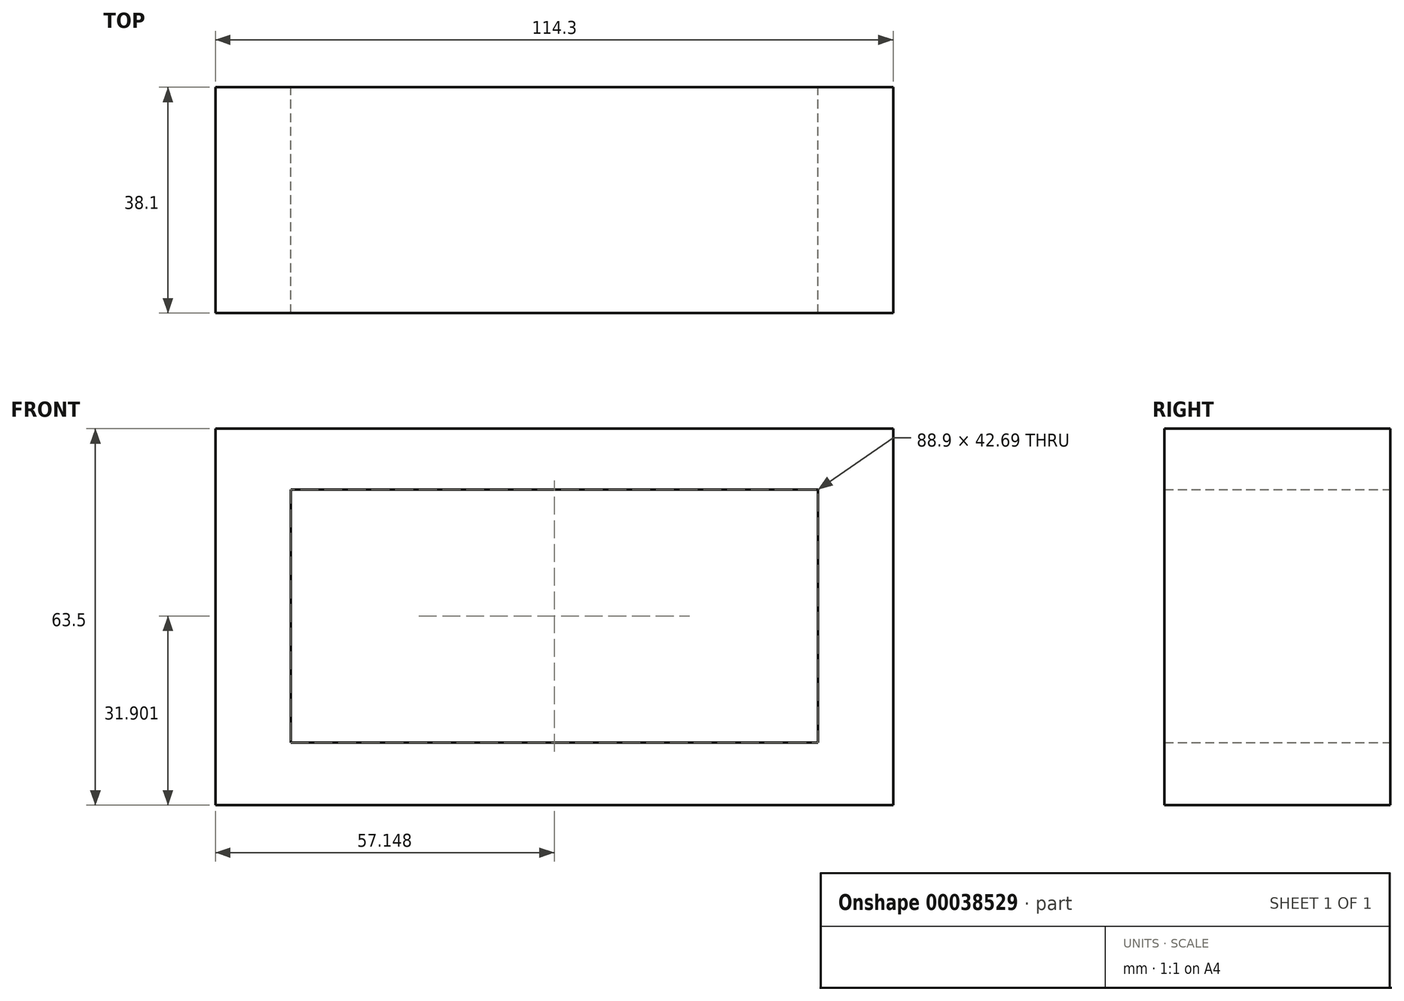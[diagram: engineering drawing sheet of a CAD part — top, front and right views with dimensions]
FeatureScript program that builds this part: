
annotation { "Feature Type Name" : "Feature", "Feature Type Description" : "" }
export const myFeature = defineFeature(function(context is Context, id is Id, definition is map)
    precondition{}
    {
        {
            var Q0;
            Q0=qCreatedBy(makeId("Front.planeOp"),FACE);
            var sketch = newSketch(context, id + "F0", { "sketchPlane" : qUnion([Q0])});
            skLineSegment(sketch, "E0.bottom", {"start": v(-61.64, 35.82) * mm, "end": v(52.66, 35.82) * mm});
            skLineSegment(sketch, "E0.top", {"start": v(-61.64, -27.68) * mm, "end": v(52.66, -27.68) * mm});
            skLineSegment(sketch, "E0.left", {"start": v(-61.64, 35.82) * mm, "end": v(-61.64, -27.68) * mm});
            skLineSegment(sketch, "E0.right", {"start": v(52.66, 35.82) * mm, "end": v(52.66, -27.68) * mm});
            skLineSegment(sketch, "E1.bottom", {"start": v(-48.94, 25.57) * mm, "end": v(39.96, 25.57) * mm});
            skLineSegment(sketch, "E1.top", {"start": v(-48.94, -17.12) * mm, "end": v(39.96, -17.12) * mm});
            skLineSegment(sketch, "E1.left", {"start": v(-48.94, 25.57) * mm, "end": v(-48.94, -17.12) * mm});
            skLineSegment(sketch, "E1.right", {"start": v(39.96, 25.57) * mm, "end": v(39.96, -17.12) * mm});
            skSolve(sketch);
        }
        {
            var Q0;
            Q0=makeQuery(id+"F0.imprint","IMPRINT",FACE,{"disambiguationData":[TD([[makeQuery(id+"F0.imprint","IMPRINT",EDGE,{"derivedFrom":sQuery(id+"F0.wireOp",EDGE,"E0.bottom")}),-1.0]])]});
            extrude(context, id + "F1", {"entities" : qUnion([Q0]), "depth" : 38.1 * mm});
        }
    });
